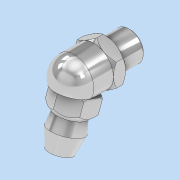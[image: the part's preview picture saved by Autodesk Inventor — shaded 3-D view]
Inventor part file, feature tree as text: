
AUTODESK INVENTOR PART (.ipt)
format: ipt  version: 2021 (Build 250183000, 183)  size: 321,024 bytes
history: native  units: mm
features: extrude x9, sketch x9, chamfer x4, projected_geometry x4, plane x3, revolve x2
ambient origin geometry x8: Origin, YZ Plane, XZ Plane, XY Plane, X Axis, Y Axis, Z Axis, Center Point
bodies: Solid1 (feature_tree)
feature tree (31):
  extrude  "Extrusion1"  Depth=0.46mm TaperAngle=0.0deg
  extrude  "Extrusion2"  Depth=4.54mm TaperAngle=0.0deg
  sketch  "Sketch4"  dims[d7=2.502mm d8=0.0mm d9=0.46mm d10=0.0mm]
  extrude  "Extrusion3"  Depth=0.46mm TaperAngle=0.0deg
  extrude  "Extrusion4"  Depth=0.62mm TaperAngle=45.0deg
  chamfer  "Chamfer1"  Distance=2.502mm
  chamfer  "Chamfer2"  Distance=4.0mm
  extrude  "Extrusion5"  Depth=4.0mm
  extrude  "Extrusion6"  TaperAngle=0.0deg  [1 undecoded]
  plane  "Work Plane1"
  revolve  "Revolution1"  [1 undecoded]
  plane  "Work Plane2"
  extrude  "Extrusion7"  Depth=5.962mm
  sketch  "Sketch9"  dims[d27=0.068mm d28=0.734mm]
  extrude  "Extrusion8"  Depth=10.0mm TaperAngle=0.0deg
  chamfer  "Chamfer3"  Distance=0.639mm
  chamfer  "Chamfer4"  Distance=8.083mm
  extrude  "Extrusion9"  Depth=3.974mm TaperAngle=0.0deg
  plane  "Work Plane3"
  revolve  "Revolution2"  Angle=45.0deg
  sketch  "Sketch1"  dims[d0=5.08mm d1=0.46mm d2=0.0mm]
  sketch  "Sketch2"  dims[d3=6.0mm d4=4.54mm d5=0.0mm]
  projected_geometry  "Projected Loop2"
  sketch  "Sketch5"  dims[d11=0.4mm d12=2.0mm d13=45.0deg d14=0.62mm d15=2.0mm d16=45.0deg d17=2.502mm d18=0.0mm]
  projected_geometry  "Projected Loop3"
  sketch  "Sketch6"  dims[d20=8.0mm d21=4.0mm d22=0.0mm]
  sketch  "Sketch7"  dims[d23=0.0mm d24=4.0mm]
  sketch  "Sketch8"  dims[d25=90.0deg d26=0.0mm]
  projected_geometry  "Projected Loop4"
  projected_geometry  "Projected Loop5"
  sketch  "Sketch11"  dims[d29=9.04mm d30=4.0mm d31=10.0mm d32=0.0mm d33=0.639mm d34=8.083mm d35=3.974mm d36=0.0mm d37=1.2mm d38=2.0mm d39=45.0deg d40=0.3mm d41=2.0mm d42=45.0deg d43=3.974mm d44=0.0mm d45=0.0mm d46=2.7625mm d47=2.7625mm d48=5.962mm d49=2.484mm d50=3.2mm d51=2.268mm d52=0.192mm d53=0.457mm d54=90.0deg]
note: 2 required parameter values undecoded (feature->parameter linkage not recoverable at this tier; creation-order binding heuristic only, values carry confidence <= 0.55)